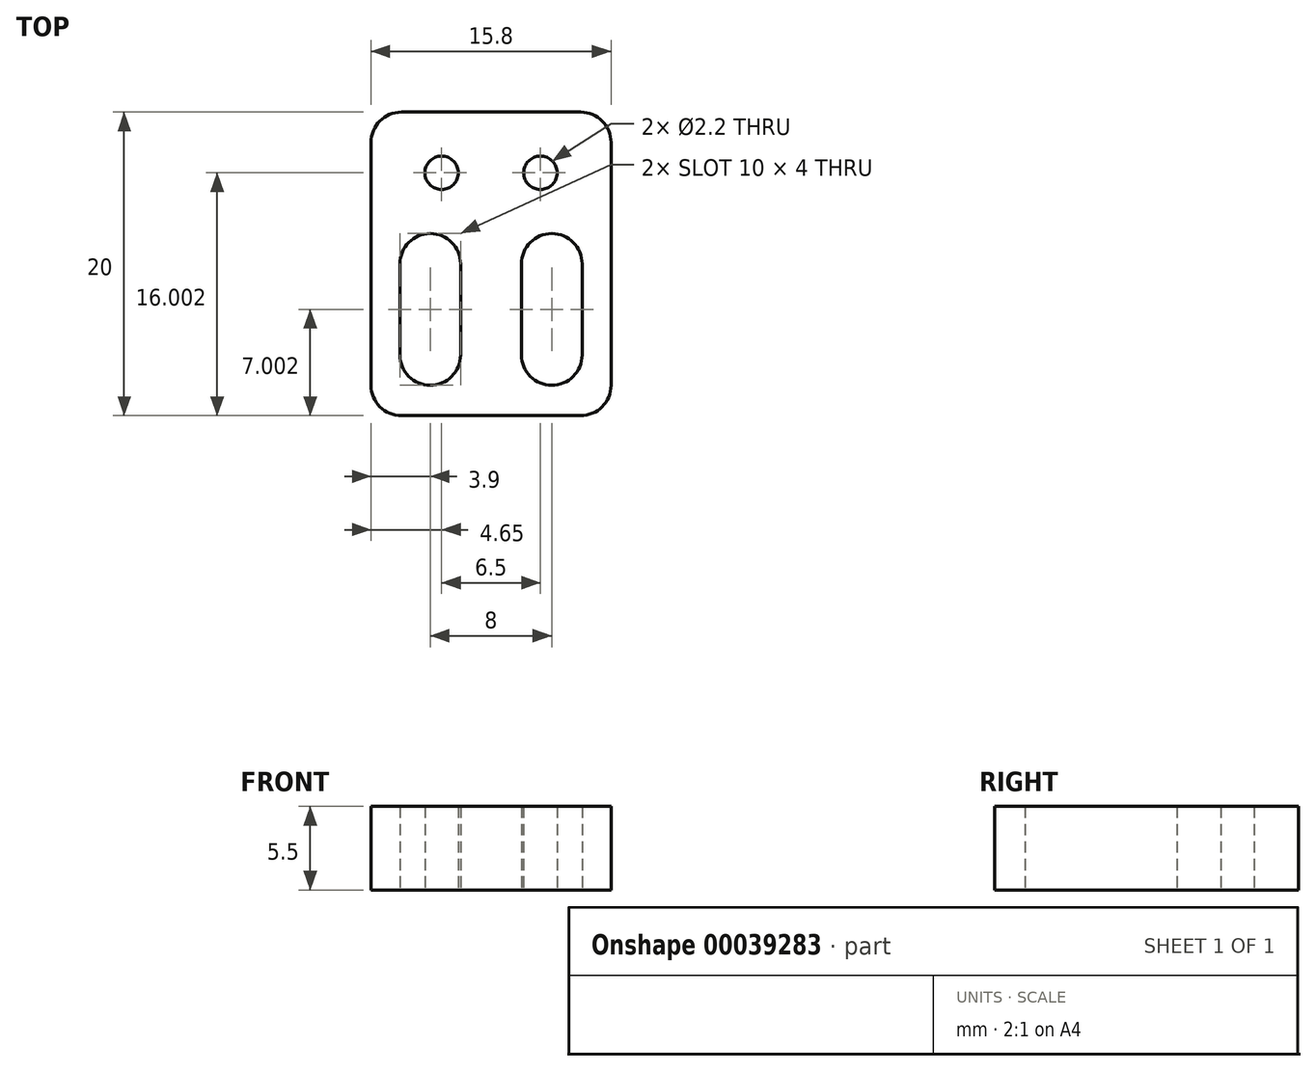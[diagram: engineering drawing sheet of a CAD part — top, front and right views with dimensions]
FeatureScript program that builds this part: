
annotation { "Feature Type Name" : "Feature", "Feature Type Description" : "" }
export const myFeature = defineFeature(function(context is Context, id is Id, definition is map)
    precondition{}
    {
        {
            var Q0;
            Q0=qCreatedBy(makeId("Top.planeOp"),FACE);
            var sketch = newSketch(context, id + "F0", { "sketchPlane" : qUnion([Q0])});
            skLineSegment(sketch, "E0.bottom", {"start": v(0, 23.83) * mm, "end": v(0, 23.83) * mm});
            skLineSegment(sketch, "E0.top", {"start": v(0, -23.13) * mm, "end": v(0, -23.13) * mm});
            skLineSegment(sketch, "E0.left", {"start": v(0, 23.83) * mm, "end": v(0, -23.13) * mm, "construction": true});
            skLineSegment(sketch, "E0.right", {"start": v(0, 23.83) * mm, "end": v(0, -23.13) * mm, "construction": true});
            skLineSegment(sketch, "E1", {"start": v(0, 5.3) * mm, "end": v(-7.9, 5.3) * mm});
            skLineSegment(sketch, "E2", {"start": v(-7.9, 5.3) * mm, "end": v(-7.9, -14.7) * mm});
            skLineSegment(sketch, "E3", {"start": v(-7.9, -14.7) * mm, "end": v(0, -14.7) * mm});
            skLineSegment(sketch, "E4.MirrorCS", {"start": v(0, 5.3) * mm, "end": v(7.9, 5.3) * mm});
            skLineSegment(sketch, "E5.MirrorCS", {"start": v(7.9, 5.3) * mm, "end": v(7.9, -14.7) * mm});
            skLineSegment(sketch, "E6.MirrorCS", {"start": v(7.9, -14.7) * mm, "end": v(0, -14.7) * mm});
            skCircle(sketch, "E7", {"center": v(-3.25, 1.3) * mm, "radius": 1.1 * mm});
            skCircle(sketch, "E8.MirrorC", {"center": v(3.25, 1.3) * mm, "radius": 1.1 * mm});
            skArc(sketch, "E9.0.startCap", {"start": v(6, -10.7) * mm, "mid": v(4, -12.7) * mm, "end": v(2, -10.7) * mm});
            skArc(sketch, "E9.0.endCap", {"start": v(2, -4.7) * mm, "mid": v(4, -2.7) * mm, "end": v(6, -4.7) * mm});
            skLineSegment(sketch, "E9.0.left", {"start": v(2, -10.7) * mm, "end": v(2, -4.7) * mm});
            skLineSegment(sketch, "E9.0.right", {"start": v(6, -10.7) * mm, "end": v(6, -4.7) * mm});
            skLineSegment(sketch, "E10.MirrorCS", {"start": v(-6, -10.7) * mm, "end": v(-6, -4.7) * mm});
            skArc(sketch, "E11.MirrorCS", {"start": v(-2, -4.7) * mm, "mid": v(-4, -2.7) * mm, "end": v(-6, -4.7) * mm});
            skLineSegment(sketch, "E12.MirrorCS", {"start": v(-2, -10.7) * mm, "end": v(-2, -4.7) * mm});
            skArc(sketch, "E13.MirrorCS", {"start": v(-6, -10.7) * mm, "mid": v(-4, -12.7) * mm, "end": v(-2, -10.7) * mm});
            skSolve(sketch);
        }
        {
            var Q0;
            Q0=makeQuery(id+"F0.imprint","IMPRINT",FACE,{"disambiguationData":[TD([[makeQuery(id+"F0.imprint","IMPRINT",EDGE,{"derivedFrom":sQuery(id+"F0.wireOp",EDGE,"E1")}),1.0]])]});
            extrude(context, id + "F1", {"entities" : qUnion([Q0]), "depth" : 5.5 * mm});
        }
        {
            var Q0;
            Q0=makeQuery(id+"F1.opExtrude","SWEPT_EDGE",EDGE,{"disambiguationData":[OSD([sQuery(id+"F0.wireOp",EDGE,"E5.MirrorCS"),sQuery(id+"F0.wireOp",EDGE,"E6.MirrorCS")])]});
            var Q1;
            Q1=makeQuery(id+"F1.opExtrude","SWEPT_EDGE",EDGE,{"disambiguationData":[OSD([sQuery(id+"F0.wireOp",EDGE,"E4.MirrorCS"),sQuery(id+"F0.wireOp",EDGE,"E5.MirrorCS")])]});
            var Q2;
            Q2=makeQuery(id+"F1.opExtrude","SWEPT_EDGE",EDGE,{"disambiguationData":[OSD([sQuery(id+"F0.wireOp",EDGE,"E2"),sQuery(id+"F0.wireOp",EDGE,"E3")])]});
            var Q3;
            Q3=makeQuery(id+"F1.opExtrude","SWEPT_EDGE",EDGE,{"disambiguationData":[OSD([sQuery(id+"F0.wireOp",EDGE,"E1"),sQuery(id+"F0.wireOp",EDGE,"E2")])]});
            fillet(context, id + "F2", {"entities" : qUnion([Q0, Q1, Q2, Q3]), "radius" : 2 * mm, "tangentPropagation" : true, "allowEdgeOverflow" : false});
        }
    });
